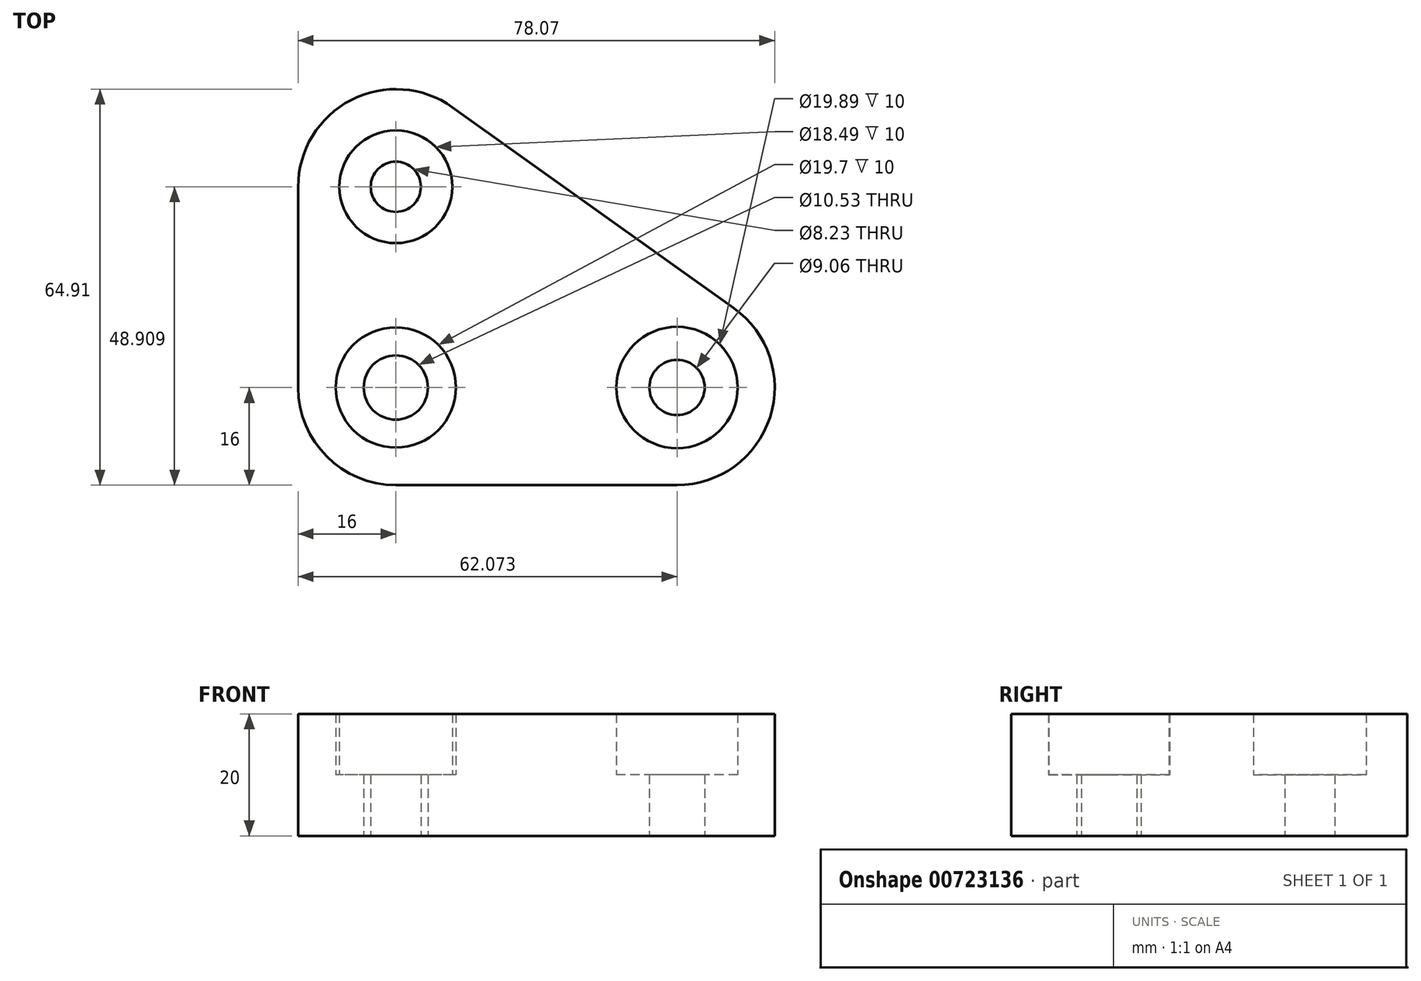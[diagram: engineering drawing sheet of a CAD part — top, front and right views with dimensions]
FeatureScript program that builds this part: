
annotation { "Feature Type Name" : "Feature", "Feature Type Description" : "" }
export const myFeature = defineFeature(function(context is Context, id is Id, definition is map)
    precondition{}
    {
        {
            var Q0;
            Q0=qCreatedBy(makeId("Top.planeOp"),FACE);
            var sketch = newSketch(context, id + "F0", { "sketchPlane" : qUnion([Q0])});
            skLineSegment(sketch, "E0.bottom", {"start": v(16, 0) * mm, "end": v(62.07, 0) * mm});
            skLineSegment(sketch, "E0.left", {"start": v(0, 16) * mm, "end": v(0, 48.9) * mm});
            skLineSegment(sketch, "E1", {"start": v(25.3, 61.93) * mm, "end": v(71.37, 29.02) * mm});
            skPoint(sketch, "E2.visualSharp", {"position": v(0, 80) * mm});
            skArc(sketch, "E2.filletArc", {"start": v(25.3, 61.93) * mm, "mid": v(8.68, 63.14) * mm, "end": v(0, 48.9) * mm});
            skPoint(sketch, "E3.visualSharp", {"position": v(112, 0) * mm});
            skArc(sketch, "E3.filletArc", {"start": v(62.07, 0) * mm, "mid": v(77.3, 11.12) * mm, "end": v(71.37, 29.02) * mm});
            skPoint(sketch, "E4.visualSharp", {"position": v(0, 0) * mm});
            skArc(sketch, "E4.filletArc", {"start": v(0, 16) * mm, "mid": v(4.69, 4.69) * mm, "end": v(16, 0) * mm});
            skCircle(sketch, "E5", {"center": v(16, 48.9) * mm, "radius": 4.12 * mm});
            skCircle(sketch, "E6", {"center": v(16, 48.9) * mm, "radius": 9.25 * mm});
            skCircle(sketch, "E7", {"center": v(62.07, 16) * mm, "radius": 4.53 * mm});
            skCircle(sketch, "E8", {"center": v(62.07, 16) * mm, "radius": 9.95 * mm});
            skCircle(sketch, "E9", {"center": v(16, 16) * mm, "radius": 5.26 * mm});
            skCircle(sketch, "E10", {"center": v(16, 16) * mm, "radius": 9.85 * mm});
            skSolve(sketch);
        }
        {
            var Q0;
            Q0=makeQuery(id+"F0.imprint","IMPRINT",FACE,{"disambiguationData":[TD([[makeQuery(id+"F0.imprint","IMPRINT",EDGE,{"derivedFrom":sQuery(id+"F0.wireOp",EDGE,"E0.bottom")}),1.0]])]});
            extrude(context, id + "F1", {"entities" : qUnion([Q0]), "depth" : 20 * mm, "offsetDistance" : 25 * mm});
        }
        {
            var Q0;
            Q0=qSketchRegion(id+"F0",true);
            var Q1;
            Q1=makeQuery(id+"F0.imprint","IMPRINT",FACE,{"disambiguationData":[TD([[makeQuery(id+"F0.imprint","IMPRINT",EDGE,{"derivedFrom":sQuery(id+"F0.wireOp",EDGE,"E5")}),-1.0]])]});
            var Q2;
            Q2=makeQuery(id+"F0.imprint","IMPRINT",FACE,{"disambiguationData":[TD([[makeQuery(id+"F0.imprint","IMPRINT",EDGE,{"derivedFrom":sQuery(id+"F0.wireOp",EDGE,"E9")}),-1.0]])]});
            var Q3;
            Q3=makeQuery(id+"F0.imprint","IMPRINT",FACE,{"disambiguationData":[TD([[makeQuery(id+"F0.imprint","IMPRINT",EDGE,{"derivedFrom":sQuery(id+"F0.wireOp",EDGE,"E7")}),-1.0]])]});
            extrude(context, id + "F2", {"entities" : qUnion([Q0, Q1, Q2, Q3]), "operationType" : NewBodyOperationType.ADD, "depth" : 10 * mm, "offsetDistance" : 25 * mm});
        }
    });
